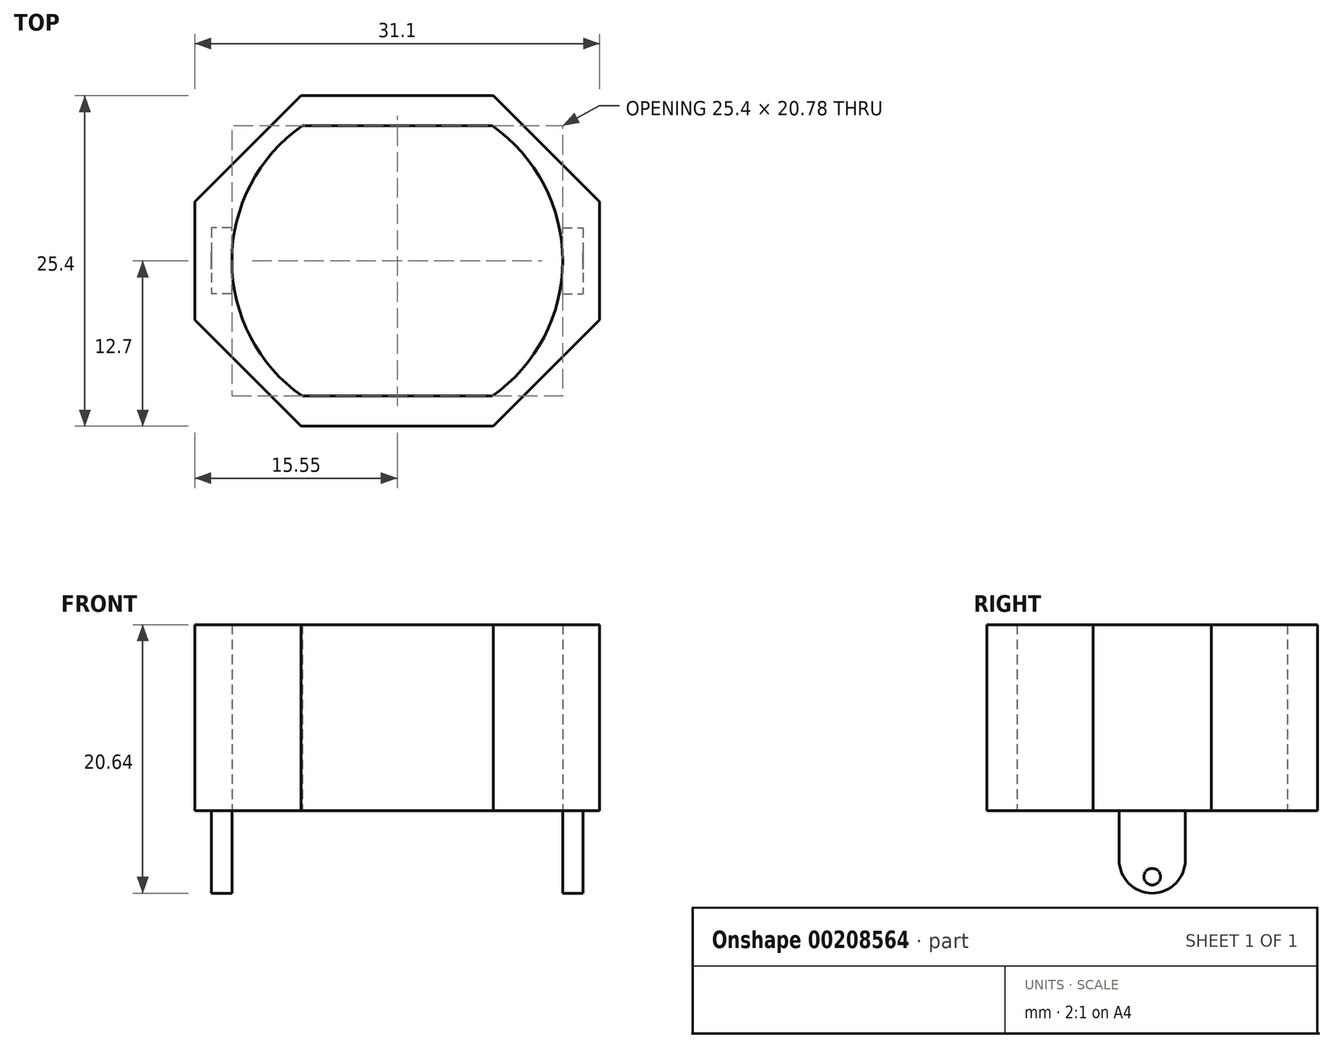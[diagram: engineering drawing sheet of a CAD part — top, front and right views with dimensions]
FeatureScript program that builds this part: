
annotation { "Feature Type Name" : "Feature", "Feature Type Description" : "" }
export const myFeature = defineFeature(function(context is Context, id is Id, definition is map)
    precondition{}
    {
        {
            var Q0;
            Q0=qCreatedBy(makeId("Top.planeOp"),FACE);
            var sketch = newSketch(context, id + "F0", { "sketchPlane" : qUnion([Q0])});
            skArc(sketch, "E0", {"start": v(12.7, 0) * mm, "mid": v(11.27, 5.85) * mm, "end": v(7.3, 10.4) * mm});
            skLineSegment(sketch, "E1", {"start": v(0, 10.4) * mm, "end": v(7.3, 10.4) * mm});
            skArc(sketch, "E2.MirrorCS", {"start": v(-12.7, 0) * mm, "mid": v(-11.27, 5.85) * mm, "end": v(-7.3, 10.4) * mm});
            skLineSegment(sketch, "E3.MirrorCS", {"start": v(0, 10.4) * mm, "end": v(-7.3, 10.4) * mm});
            skLineSegment(sketch, "E4.MirrorCS", {"start": v(0, -10.4) * mm, "end": v(7.3, -10.4) * mm});
            skArc(sketch, "E5.MirrorCS", {"start": v(-12.7, 0) * mm, "mid": v(-11.27, -5.85) * mm, "end": v(-7.3, -10.4) * mm});
            skLineSegment(sketch, "E6.MirrorCS", {"start": v(0, -10.4) * mm, "end": v(-7.3, -10.4) * mm});
            skArc(sketch, "E7.MirrorCS", {"start": v(12.7, 0) * mm, "mid": v(11.27, -5.85) * mm, "end": v(7.3, -10.4) * mm});
            skLineSegment(sketch, "E8", {"start": v(0, 12.7) * mm, "end": v(7.39, 12.7) * mm});
            skLineSegment(sketch, "E9", {"start": v(7.39, 12.7) * mm, "end": v(15.55, 4.54) * mm});
            skLineSegment(sketch, "E10", {"start": v(15.55, 4.54) * mm, "end": v(15.55, 0) * mm});
            skLineSegment(sketch, "E11.MirrorCS", {"start": v(-7.39, 12.7) * mm, "end": v(-15.55, 4.54) * mm});
            skLineSegment(sketch, "E12.MirrorCS", {"start": v(0, 12.7) * mm, "end": v(-7.39, 12.7) * mm});
            skLineSegment(sketch, "E13.MirrorCS", {"start": v(-15.55, 4.54) * mm, "end": v(-15.55, 0) * mm});
            skLineSegment(sketch, "E14.MirrorCS", {"start": v(15.55, -4.54) * mm, "end": v(15.55, 0) * mm});
            skLineSegment(sketch, "E15.MirrorCS", {"start": v(7.39, -12.7) * mm, "end": v(15.55, -4.54) * mm});
            skLineSegment(sketch, "E16.MirrorCS", {"start": v(0, -12.7) * mm, "end": v(7.39, -12.7) * mm});
            skLineSegment(sketch, "E17.MirrorCS", {"start": v(0, -12.7) * mm, "end": v(-7.39, -12.7) * mm});
            skLineSegment(sketch, "E18.MirrorCS", {"start": v(-7.39, -12.7) * mm, "end": v(-15.55, -4.54) * mm});
            skLineSegment(sketch, "E19.MirrorCS", {"start": v(-15.55, -4.54) * mm, "end": v(-15.55, 0) * mm});
            skSolve(sketch);
        }
        {
            var Q0;
            Q0=makeQuery(id+"F0.imprint","IMPRINT",FACE,{"disambiguationData":[TD([[makeQuery(id+"F0.imprint","IMPRINT",EDGE,{"derivedFrom":sQuery(id+"F0.wireOp",EDGE,"E0")}),-1.0]])]});
            extrude(context, id + "F1", {"entities" : qUnion([Q0]), "depth" : 28.57 * mm});
        }
        {
            var Q0;
            Q0=qCreatedBy(makeId("Top.planeOp"),FACE);
            var sketch = newSketch(context, id + "F2", { "sketchPlane" : qUnion([Q0])});
            skPoint(sketch, "E20", {"position": v(12.7, 0) * mm});
            skLineSegment(sketch, "E21", {"start": v(14.27, 0) * mm, "end": v(14.27, 2.54) * mm});
            skLineSegment(sketch, "E22", {"start": v(12.7, 2.54) * mm, "end": v(14.27, 2.54) * mm});
            skLineSegment(sketch, "E23.MirrorCS", {"start": v(12.7, 0) * mm, "end": v(12.7, -2.54) * mm});
            skLineSegment(sketch, "E24.MirrorCS", {"start": v(14.27, 0) * mm, "end": v(14.27, -2.54) * mm});
            skLineSegment(sketch, "E25.MirrorCS", {"start": v(12.7, -2.54) * mm, "end": v(14.27, -2.54) * mm});
            skLineSegment(sketch, "E26", {"start": v(12.7, 0) * mm, "end": v(12.7, 2.54) * mm});
            skSolve(sketch);
        }
        {
            var Q0;
            Q0=makeQuery(id+"F2.imprint","IMPRINT",FACE,{"disambiguationData":[TD([[makeQuery(id+"F2.imprint","IMPRINT",EDGE,{"derivedFrom":sQuery(id+"F2.wireOp",EDGE,"E21")}),1.0]])]});
            extrude(context, id + "F3", {"entities" : qUnion([Q0]), "operationType" : NewBodyOperationType.ADD, "oppositeDirection" : true, "depth" : 6.35 * mm});
        }
        {
            var Q0;
            Q0=makeQuery(id+"F3.opExtrude","SWEPT_FACE",FACE,{"disambiguationData":[OSD([sQuery(id+"F2.wireOp",EDGE,"E21"),sQuery(id+"F2.wireOp",EDGE,"E24.MirrorCS")])]});
            var sketch = newSketch(context, id + "F4", { "sketchPlane" : qUnion([Q0])});
            skCircle(sketch, "E27", {"center": v(0, -5.08) * mm, "radius": 0.64 * mm});
            skPoint(sketch, "E27.centerSnap0", {"position": v(0, -6.35) * mm});
            skSolve(sketch);
        }
        {
            var Q0;
            Q0=makeQuery(id+"F4.imprint","IMPRINT",FACE,{"disambiguationData":[TD([[makeQuery(id+"F4.imprint","IMPRINT",EDGE,{"derivedFrom":sQuery(id+"F4.wireOp",EDGE,"E27")}),1.0]])]});
            extrude(context, id + "F5", {"entities" : qUnion([Q0]), "operationType" : NewBodyOperationType.ADD, "depth" : 0.12 / 50.8 * mm});
        }
        {
            var Q0;
            Q0=makeQuery(id+"FM54qVA6fSZPACi_2.opPattern","COPY",EDGE,{"derivedFrom":makeQuery(id+"F3.opExtrude","CAP_EDGE",EDGE,{"disambiguationData":[OSD([sQuery(id+"F2.wireOp",EDGE,"E25.MirrorCS")])],"isStart":false}),"instanceName":"1"});
            var Q1;
            Q1=makeQuery(id+"FM54qVA6fSZPACi_2.opPattern","COPY",EDGE,{"derivedFrom":makeQuery(id+"F3.opExtrude","CAP_EDGE",EDGE,{"disambiguationData":[OSD([sQuery(id+"F2.wireOp",EDGE,"E22")])],"isStart":false}),"instanceName":"1"});
            var Q2;
            Q2=makeQuery(id+"F3.opExtrude","CAP_EDGE",EDGE,{"disambiguationData":[OSD([sQuery(id+"F2.wireOp",EDGE,"E25.MirrorCS")])],"isStart":false});
            var Q3;
            Q3=makeQuery(id+"F3.opExtrude","CAP_EDGE",EDGE,{"disambiguationData":[OSD([sQuery(id+"F2.wireOp",EDGE,"E22")])],"isStart":false});
            fillet(context, id + "F6", {"entities" : qUnion([Q0, Q1, Q2, Q3]), "radius" : 2.54 * mm, "tangentPropagation" : true, "allowEdgeOverflow" : false});
        }
        {
            var Q0;
            Q0=makeQuery(id+"F5.opExtrude","CAP_EDGE",EDGE,{"disambiguationData":[OSD([sQuery(id+"F4.wireOp",EDGE,"E27")])],"isStart":false});
            var Q1;
            Q1=makeQuery(id+"FM54qVA6fSZPACi_2.opPattern","COPY",EDGE,{"derivedFrom":makeQuery(id+"F5.opExtrude","CAP_EDGE",EDGE,{"disambiguationData":[OSD([sQuery(id+"F4.wireOp",EDGE,"E27")])],"isStart":false}),"instanceName":"1"});
            fillet(context, id + "F7", {"entities" : qUnion([Q0, Q1]), "radius" : 0.64 * mm, "tangentPropagation" : true, "allowEdgeOverflow" : false});
        }
        {
            var Q0;
            Q0=makeQuery(id+"F1.opExtrude","CAP_FACE",FACE,{"disambiguationData":[OSD([sQuery(id+"F0.wireOp",EDGE,"E0"),sQuery(id+"F0.wireOp",EDGE,"E1"),sQuery(id+"F0.wireOp",EDGE,"E2.MirrorCS"),sQuery(id+"F0.wireOp",EDGE,"E3.MirrorCS"),sQuery(id+"F0.wireOp",EDGE,"E4.MirrorCS"),sQuery(id+"F0.wireOp",EDGE,"E5.MirrorCS"),sQuery(id+"F0.wireOp",EDGE,"E6.MirrorCS"),sQuery(id+"F0.wireOp",EDGE,"E7.MirrorCS"),sQuery(id+"F0.wireOp",EDGE,"E8"),sQuery(id+"F0.wireOp",EDGE,"E9"),sQuery(id+"F0.wireOp",EDGE,"E10"),sQuery(id+"F0.wireOp",EDGE,"E11.MirrorCS"),sQuery(id+"F0.wireOp",EDGE,"E12.MirrorCS"),sQuery(id+"F0.wireOp",EDGE,"E13.MirrorCS"),sQuery(id+"F0.wireOp",EDGE,"E14.MirrorCS"),sQuery(id+"F0.wireOp",EDGE,"E15.MirrorCS"),sQuery(id+"F0.wireOp",EDGE,"E16.MirrorCS"),sQuery(id+"F0.wireOp",EDGE,"E17.MirrorCS"),sQuery(id+"F0.wireOp",EDGE,"E18.MirrorCS"),sQuery(id+"F0.wireOp",EDGE,"E19.MirrorCS")])],"isStart":false});
            var sketch = newSketch(context, id + "F8", { "sketchPlane" : qUnion([Q0])});
            skPoint(sketch, "E28", {"position": v(13.98, 2.54) * mm});
            skPoint(sketch, "E29", {"position": v(15.55, 0) * mm});
            skLineSegment(sketch, "E30.bottom", {"start": v(13.98, 2.54) * mm, "end": v(15.55, 2.54) * mm});
            skLineSegment(sketch, "E30.left", {"start": v(13.98, 2.54) * mm, "end": v(13.98, 0) * mm});
            skLineSegment(sketch, "E30.right", {"start": v(15.55, 2.54) * mm, "end": v(15.55, 0) * mm});
            skLineSegment(sketch, "E31.MirrorCS", {"start": v(15.55, -2.54) * mm, "end": v(15.55, 0) * mm});
            skLineSegment(sketch, "E32.MirrorCS", {"start": v(13.98, -2.54) * mm, "end": v(15.55, -2.54) * mm});
            skLineSegment(sketch, "E33.MirrorCS", {"start": v(13.98, -2.54) * mm, "end": v(13.98, 0) * mm});
            skSolve(sketch);
        }
        {
            var Q0;
            Q0=makeQuery(id+"F8.imprint","IMPRINT",FACE,{"disambiguationData":[TD([[makeQuery(id+"F8.imprint","IMPRINT",EDGE,{"derivedFrom":sQuery(id+"F8.wireOp",EDGE,"E30.bottom")}),-1.0]])]});
            extrude(context, id + "F9", {"entities" : qUnion([Q0]), "operationType" : NewBodyOperationType.ADD, "depth" : 6.35 * mm});
        }
        {
            var Q0;
            Q0=makeQuery(id+"F9.boolean.opBoolean","MERGE",FACE,{"derivedFrom":[makeQuery(id+"F1.opExtrude","SWEPT_FACE",FACE,{"disambiguationData":[OSD([sQuery(id+"F0.wireOp",EDGE,"E10"),sQuery(id+"F0.wireOp",EDGE,"E14.MirrorCS")])]}),makeQuery(id+"F9.opExtrude","SWEPT_FACE",FACE,{"disambiguationData":[OSD([sQuery(id+"F8.wireOp",EDGE,"E30.right"),sQuery(id+"F8.wireOp",EDGE,"E31.MirrorCS")])]})]});
            var sketch = newSketch(context, id + "F10", { "sketchPlane" : qUnion([Q0])});
            skPoint(sketch, "E34", {"position": v(0, 32.39) * mm});
            skPoint(sketch, "E34.positionSnap0", {"position": v(0, 34.93) * mm});
            skSolve(sketch);
        }
        {
            var Q0;
            Q0=sQuery(id+"F10.wireOp",VERTEX,"E34");
            var Q1;
            Q1=makeQuery(id+"F1.opExtrude","SWEPT_BODY",BODY,{"disambiguationData":[OSD([sQuery(id+"F0.wireOp",EDGE,"E0"),sQuery(id+"F0.wireOp",EDGE,"E1"),sQuery(id+"F0.wireOp",EDGE,"E2.MirrorCS"),sQuery(id+"F0.wireOp",EDGE,"E3.MirrorCS"),sQuery(id+"F0.wireOp",EDGE,"E4.MirrorCS"),sQuery(id+"F0.wireOp",EDGE,"E5.MirrorCS"),sQuery(id+"F0.wireOp",EDGE,"E6.MirrorCS"),sQuery(id+"F0.wireOp",EDGE,"E7.MirrorCS"),sQuery(id+"F0.wireOp",EDGE,"E8"),sQuery(id+"F0.wireOp",EDGE,"E9"),sQuery(id+"F0.wireOp",EDGE,"E10"),sQuery(id+"F0.wireOp",EDGE,"E11.MirrorCS"),sQuery(id+"F0.wireOp",EDGE,"E12.MirrorCS"),sQuery(id+"F0.wireOp",EDGE,"E13.MirrorCS"),sQuery(id+"F0.wireOp",EDGE,"E14.MirrorCS"),sQuery(id+"F0.wireOp",EDGE,"E15.MirrorCS"),sQuery(id+"F0.wireOp",EDGE,"E16.MirrorCS"),sQuery(id+"F0.wireOp",EDGE,"E17.MirrorCS"),sQuery(id+"F0.wireOp",EDGE,"E18.MirrorCS"),sQuery(id+"F0.wireOp",EDGE,"E19.MirrorCS")])]});
            hole(context, id + "F11", {"style" : HoleStyle.SIMPLE, "endStyle" : HoleEndStyle.THROUGH, "holeDiameter" : 2.54 * mm, "locations" : qUnion([Q0]), "scope" : qUnion([Q1]), "isTappedThrough" : true});
        }
        {
            var Q0;
            Q0=makeQuery(id+"F1.opExtrude","SWEPT_BODY",BODY,{"disambiguationData":[OSD([sQuery(id+"F0.wireOp",EDGE,"E0"),sQuery(id+"F0.wireOp",EDGE,"E1"),sQuery(id+"F0.wireOp",EDGE,"E2.MirrorCS"),sQuery(id+"F0.wireOp",EDGE,"E3.MirrorCS"),sQuery(id+"F0.wireOp",EDGE,"E4.MirrorCS"),sQuery(id+"F0.wireOp",EDGE,"E5.MirrorCS"),sQuery(id+"F0.wireOp",EDGE,"E6.MirrorCS"),sQuery(id+"F0.wireOp",EDGE,"E7.MirrorCS"),sQuery(id+"F0.wireOp",EDGE,"E8"),sQuery(id+"F0.wireOp",EDGE,"E9"),sQuery(id+"F0.wireOp",EDGE,"E10"),sQuery(id+"F0.wireOp",EDGE,"E11.MirrorCS"),sQuery(id+"F0.wireOp",EDGE,"E12.MirrorCS"),sQuery(id+"F0.wireOp",EDGE,"E13.MirrorCS"),sQuery(id+"F0.wireOp",EDGE,"E14.MirrorCS"),sQuery(id+"F0.wireOp",EDGE,"E15.MirrorCS"),sQuery(id+"F0.wireOp",EDGE,"E16.MirrorCS"),sQuery(id+"F0.wireOp",EDGE,"E17.MirrorCS"),sQuery(id+"F0.wireOp",EDGE,"E18.MirrorCS"),sQuery(id+"F0.wireOp",EDGE,"E19.MirrorCS")])]});
            var Q1;
            Q1=qCreatedBy(makeId("Right.planeOp"),FACE);
            mirror(context, id + "F12", {"operationType" : NewBodyOperationType.ADD, "entities" : qUnion([Q0]), "mirrorPlane" : qUnion([Q1])});
        }
        {
            var Q0;
            Q0=makeQuery(id+"F1.opExtrude","SWEPT_FACE",FACE,{"disambiguationData":[OSD([sQuery(id+"F0.wireOp",EDGE,"E1"),sQuery(id+"F0.wireOp",EDGE,"E3.MirrorCS")])]});
            var sketch = newSketch(context, id + "F13", { "sketchPlane" : qUnion([Q0])});
            skLineSegment(sketch, "E35", {"start": v(7.3, 14.29) * mm, "end": v(-7.3, 14.29) * mm});
            skSolve(sketch);
        }
        {
            var Q0;
            Q0=sQuery(id+"F13.wireOp",EDGE,"E35");
            extrude(context, id + "F14", {"bodyType" : ToolBodyType.SURFACE, "surfaceEntities" : qUnion([Q0]), "endBound" : BoundingType.UP_TO_NEXT, "depth" : 25.4 * mm});
        }
        {
            var Q0;
            Q0=makeQuery(id+"F14.opExtrude","SWEPT_FACE",FACE,{"disambiguationData":[OSD([sQuery(id+"F13.wireOp",EDGE,"E35")])]});
            var sketch = newSketch(context, id + "F15", { "sketchPlane" : qUnion([Q0])});
            skPoint(sketch, "E36", {"position": v(0, 0) * mm});
            skSolve(sketch);
        }
        {
            var Q0;
            Q0=sQuery(id+"F15.wireOp",VERTEX,"E36");
            var Q1;
            Q1=makeQuery(id+"F1.opExtrude","SWEPT_BODY",BODY,{"disambiguationData":[OSD([sQuery(id+"F0.wireOp",EDGE,"E0"),sQuery(id+"F0.wireOp",EDGE,"E1"),sQuery(id+"F0.wireOp",EDGE,"E2.MirrorCS"),sQuery(id+"F0.wireOp",EDGE,"E3.MirrorCS"),sQuery(id+"F0.wireOp",EDGE,"E4.MirrorCS"),sQuery(id+"F0.wireOp",EDGE,"E5.MirrorCS"),sQuery(id+"F0.wireOp",EDGE,"E6.MirrorCS"),sQuery(id+"F0.wireOp",EDGE,"E7.MirrorCS"),sQuery(id+"F0.wireOp",EDGE,"E8"),sQuery(id+"F0.wireOp",EDGE,"E9"),sQuery(id+"F0.wireOp",EDGE,"E10"),sQuery(id+"F0.wireOp",EDGE,"E11.MirrorCS"),sQuery(id+"F0.wireOp",EDGE,"E12.MirrorCS"),sQuery(id+"F0.wireOp",EDGE,"E13.MirrorCS"),sQuery(id+"F0.wireOp",EDGE,"E14.MirrorCS"),sQuery(id+"F0.wireOp",EDGE,"E15.MirrorCS"),sQuery(id+"F0.wireOp",EDGE,"E16.MirrorCS"),sQuery(id+"F0.wireOp",EDGE,"E17.MirrorCS"),sQuery(id+"F0.wireOp",EDGE,"E18.MirrorCS"),sQuery(id+"F0.wireOp",EDGE,"E19.MirrorCS")])]});
            hole(context, id + "F16", {"style" : HoleStyle.SIMPLE, "endStyle" : HoleEndStyle.THROUGH, "oppositeDirection" : true, "holeDiameter" : 127 * mm, "locations" : qUnion([Q0]), "scope" : qUnion([Q1]), "isTappedThrough" : true});
        }
        {
            var Q0;
            Q0=makeQuery(id+"F14.opExtrude","SWEPT_BODY",BODY,{"disambiguationData":[OSD([sQuery(id+"F13.wireOp",EDGE,"E35")])]});
            deleteBodies(context, id + "F17", {"entities" : qUnion([Q0])});
        }
    });
